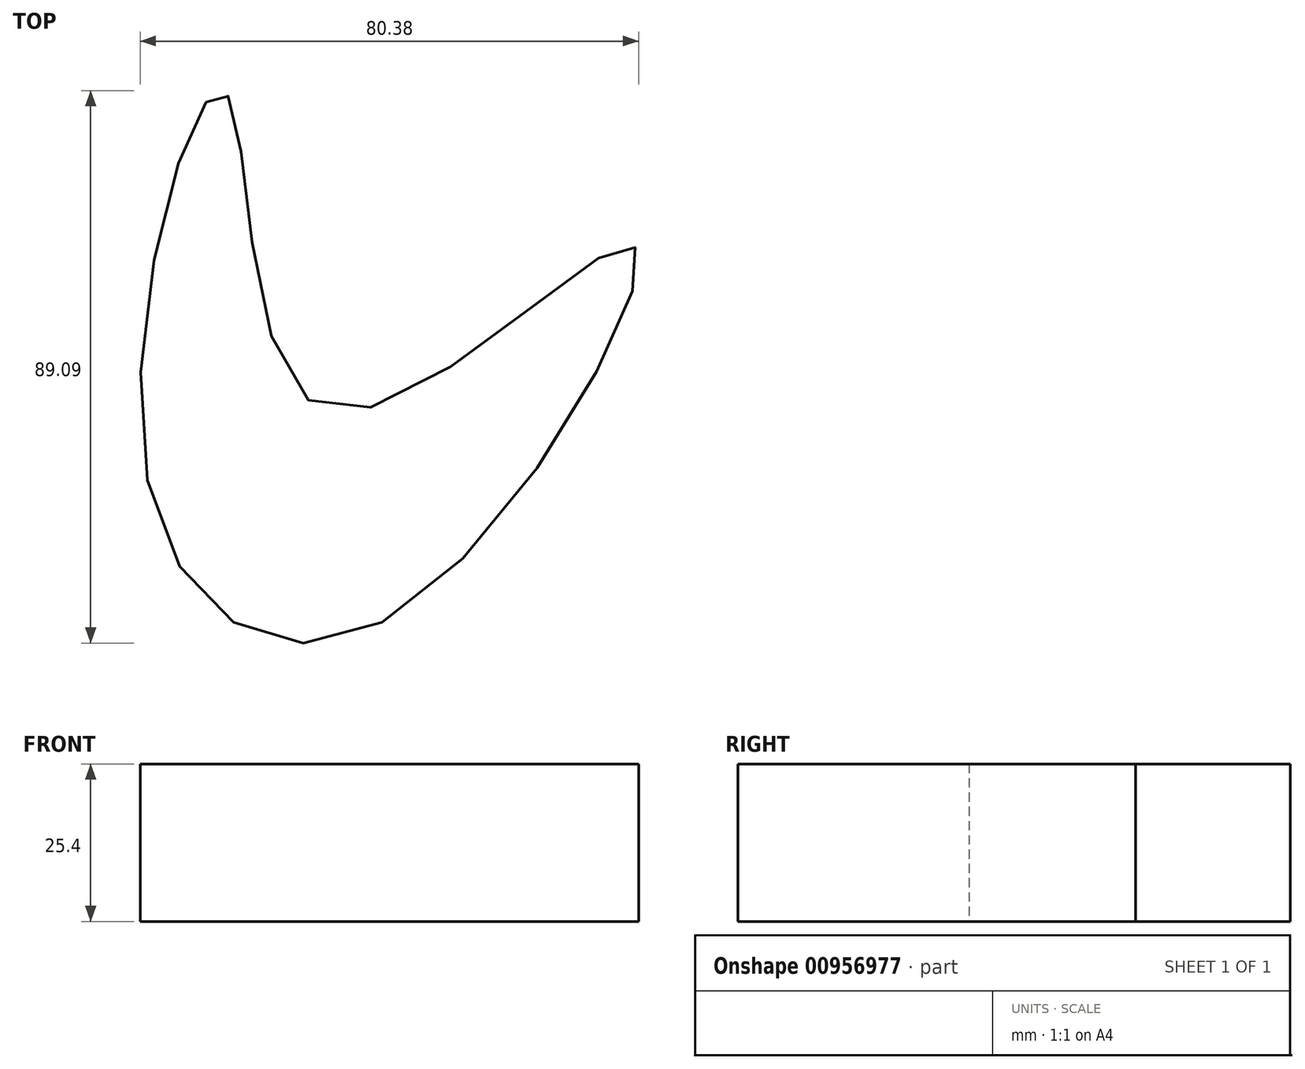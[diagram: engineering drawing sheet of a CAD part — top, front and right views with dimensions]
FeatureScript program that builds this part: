
annotation { "Feature Type Name" : "Feature", "Feature Type Description" : "" }
export const myFeature = defineFeature(function(context is Context, id is Id, definition is map)
    precondition{}
    {
        {
            var Q0;
            Q0=qCreatedBy(makeId("Top.planeOp"),FACE);
            var sketch = newSketch(context, id + "F0", { "sketchPlane" : qUnion([Q0])});
            skFitSpline(sketch, "E0", {"points": [v(-43.42, -37.9) * mm, v(-30.84, 24.64) * mm, v(-15.27, -26.25) * mm, v(34.63, 0) * mm, v(-5.05, -60.49) * mm, v(-43.42, -37.9) * mm]});
            skSolve(sketch);
        }
        {
            var Q0;
            Q0 = qSketchRegion(id + "F0", true);
            extrude(context, id + "F1", {"entities" : qUnion([Q0]), "depth" : 25.4 * mm, "offsetDistance" : 25.4 * mm});
        }
    });
